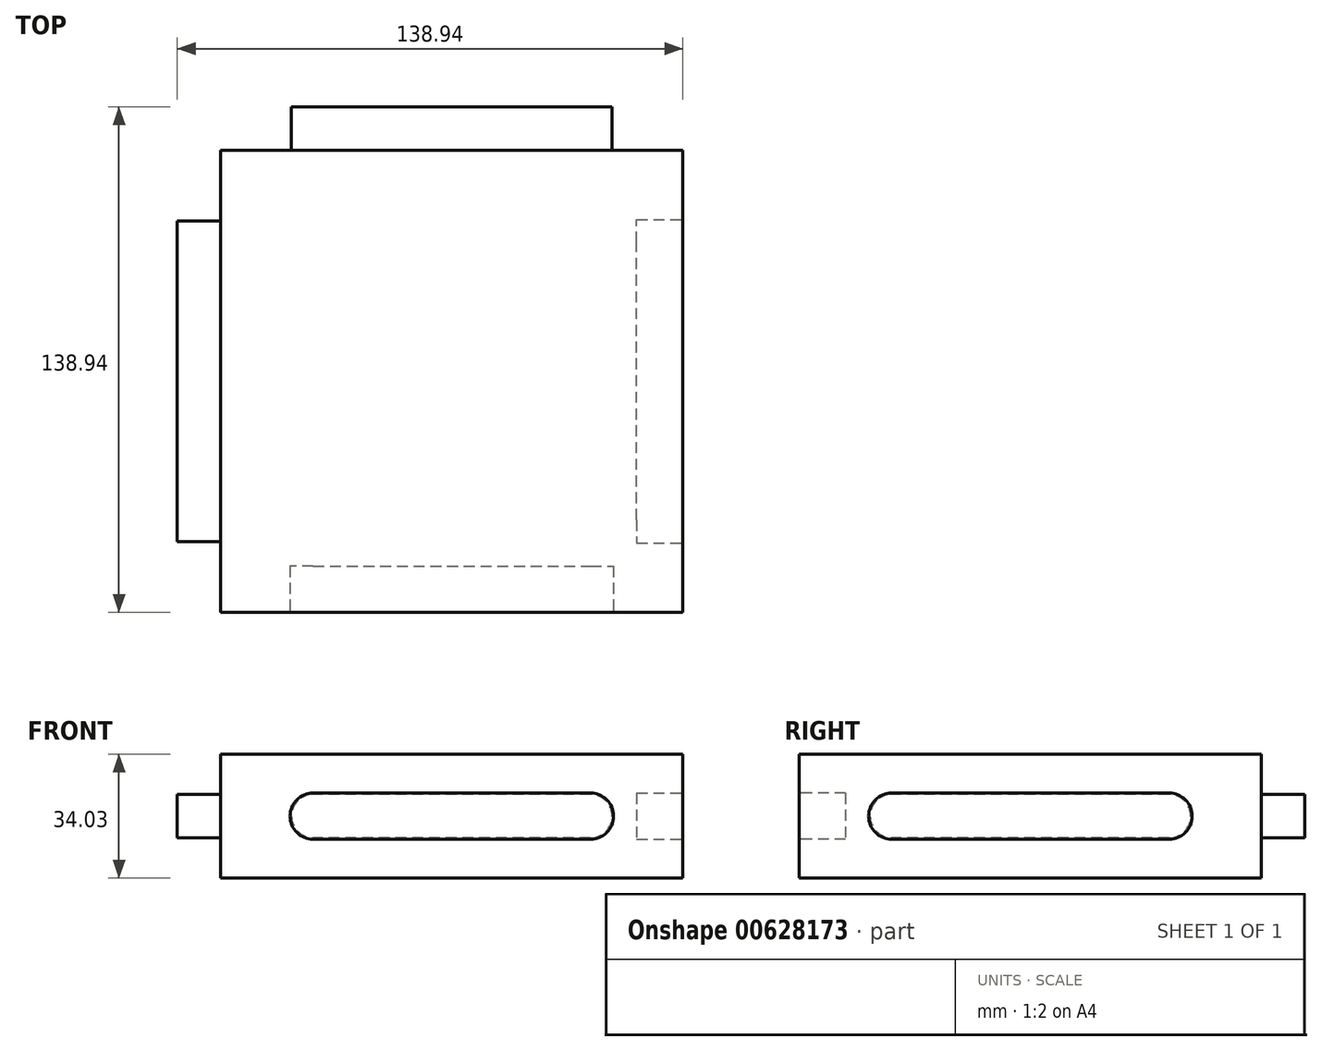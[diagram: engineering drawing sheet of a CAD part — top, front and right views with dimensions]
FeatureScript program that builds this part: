
annotation { "Feature Type Name" : "Feature", "Feature Type Description" : "" }
export const myFeature = defineFeature(function(context is Context, id is Id, definition is map)
    precondition{}
    {
        {
            var Q0;
            Q0=qCreatedBy(makeId("Top.planeOp"),FACE);
            var sketch = newSketch(context, id + "F0", { "sketchPlane" : qUnion([Q0])});
            skLineSegment(sketch, "E0.bottom", {"start": v(-63.5, 63.5) * mm, "end": v(63.5, 63.5) * mm});
            skLineSegment(sketch, "E0.top", {"start": v(-63.5, -63.5) * mm, "end": v(63.5, -63.5) * mm});
            skLineSegment(sketch, "E0.left", {"start": v(-63.5, 63.5) * mm, "end": v(-63.5, -63.5) * mm});
            skLineSegment(sketch, "E0.right", {"start": v(63.5, 63.5) * mm, "end": v(63.5, -63.5) * mm});
            skSolve(sketch);
        }
        {
            var Q0;
            Q0 = qSketchRegion(id + "F0", true);
            extrude(context, id + "F1", {"entities" : qUnion([Q0]), "depth" : 34.03 * mm, "offsetDistance" : 25.4 * mm});
        }
        {
            var Q0;
            Q0=makeQuery(id+"F1.opExtrude","SWEPT_FACE",FACE,{"disambiguationData":[OSD([sQuery(id+"F0.wireOp",EDGE,"E0.bottom")])]});
            var sketch = newSketch(context, id + "F2", { "sketchPlane" : qUnion([Q0])});
            skLineSegment(sketch, "E1", {"start": v(-63.5, 17.01) * mm, "end": v(-38.1, 17.01) * mm, "construction": true});
            skLineSegment(sketch, "E2", {"start": v(63.5, 17.01) * mm, "end": v(38.1, 17.01) * mm, "construction": true});
            skLineSegment(sketch, "E3", {"start": v(-38.1, 17.01) * mm, "end": v(38.1, 17.01) * mm, "construction": true});
            skArc(sketch, "E4.0.startCap", {"start": v(-38.1, 11.05) * mm, "mid": v(-44.07, 17.01) * mm, "end": v(-38.1, 22.98) * mm});
            skArc(sketch, "E4.0.endCap", {"start": v(38.1, 22.98) * mm, "mid": v(44.07, 17.01) * mm, "end": v(38.1, 11.05) * mm});
            skLineSegment(sketch, "E4.0.left", {"start": v(-38.1, 22.98) * mm, "end": v(38.1, 22.98) * mm});
            skLineSegment(sketch, "E4.0.right", {"start": v(-38.1, 11.05) * mm, "end": v(38.1, 11.05) * mm});
            skSolve(sketch);
        }
        {
            var Q0;
            Q0 = qSketchRegion(id + "F2", true);
            extrude(context, id + "F3", {"entities" : qUnion([Q0]), "operationType" : NewBodyOperationType.ADD, "depth" : 11.94 * mm, "offsetDistance" : 25.4 * mm});
        }
        {
            var Q0;
            Q0=makeQuery(id+"F1.opExtrude","SWEPT_FACE",FACE,{"disambiguationData":[OSD([sQuery(id+"F0.wireOp",EDGE,"E0.right")])]});
            var sketch = newSketch(context, id + "F4", { "sketchPlane" : qUnion([Q0])});
            skLineSegment(sketch, "E5", {"start": v(-63.5, 17.01) * mm, "end": v(-38.1, 17.01) * mm, "construction": true});
            skLineSegment(sketch, "E6", {"start": v(63.5, 17.01) * mm, "end": v(38.1, 17.01) * mm, "construction": true});
            skLineSegment(sketch, "E7", {"start": v(-38.1, 17.01) * mm, "end": v(38.1, 17.01) * mm, "construction": true});
            skArc(sketch, "E8.0.startCap", {"start": v(-38.1, 10.66) * mm, "mid": v(-44.45, 17.01) * mm, "end": v(-38.1, 23.36) * mm});
            skArc(sketch, "E8.0.endCap", {"start": v(38.1, 23.36) * mm, "mid": v(44.45, 17.01) * mm, "end": v(38.1, 10.66) * mm});
            skLineSegment(sketch, "E8.0.left", {"start": v(-38.1, 23.36) * mm, "end": v(38.1, 23.36) * mm});
            skLineSegment(sketch, "E8.0.right", {"start": v(-38.1, 10.66) * mm, "end": v(38.1, 10.66) * mm});
            skSolve(sketch);
        }
        {
            var Q0;
            Q0=makeQuery(id+"F1.opExtrude","SWEPT_FACE",FACE,{"disambiguationData":[OSD([sQuery(id+"F0.wireOp",EDGE,"E0.top")])]});
            var sketch = newSketch(context, id + "F5", { "sketchPlane" : qUnion([Q0])});
            skLineSegment(sketch, "E9", {"start": v(-63.5, 17.01) * mm, "end": v(-38.1, 17.01) * mm, "construction": true});
            skLineSegment(sketch, "E10", {"start": v(63.5, 17.01) * mm, "end": v(38.1, 17.01) * mm, "construction": true});
            skLineSegment(sketch, "E11", {"start": v(-38.1, 17.01) * mm, "end": v(38.1, 17.01) * mm, "construction": true});
            skArc(sketch, "E12.0.startCap", {"start": v(-38.1, 10.66) * mm, "mid": v(-44.45, 17.01) * mm, "end": v(-38.1, 23.36) * mm});
            skArc(sketch, "E12.0.endCap", {"start": v(38.1, 23.36) * mm, "mid": v(44.45, 17.01) * mm, "end": v(38.1, 10.66) * mm});
            skLineSegment(sketch, "E12.0.left", {"start": v(-38.1, 23.36) * mm, "end": v(38.1, 23.36) * mm});
            skLineSegment(sketch, "E12.0.right", {"start": v(-38.1, 10.66) * mm, "end": v(38.1, 10.66) * mm});
            skSolve(sketch);
        }
        {
            var Q0;
            Q0 = qSketchRegion(id + "F4", true);
            extrude(context, id + "F6", {"entities" : qUnion([Q0]), "operationType" : NewBodyOperationType.REMOVE, "oppositeDirection" : true, "depth" : 12.7 * mm, "offsetDistance" : 25.4 * mm});
        }
        {
            var Q0;
            Q0 = qSketchRegion(id + "F5", true);
            extrude(context, id + "F7", {"entities" : qUnion([Q0]), "operationType" : NewBodyOperationType.REMOVE, "oppositeDirection" : true, "depth" : 12.7 * mm, "offsetDistance" : 25.4 * mm});
        }
        {
            var Q0;
            Q0=makeQuery(id+"F1.opExtrude","SWEPT_FACE",FACE,{"disambiguationData":[OSD([sQuery(id+"F0.wireOp",EDGE,"E0.left")])]});
            var sketch = newSketch(context, id + "F8", { "sketchPlane" : qUnion([Q0])});
            skLineSegment(sketch, "E13", {"start": v(-63.5, 17.01) * mm, "end": v(-38.1, 17.01) * mm, "construction": true});
            skLineSegment(sketch, "E14", {"start": v(63.5, 17.01) * mm, "end": v(38.1, 17.01) * mm, "construction": true});
            skLineSegment(sketch, "E15", {"start": v(-38.1, 17.01) * mm, "end": v(38.1, 17.01) * mm, "construction": true});
            skArc(sketch, "E16.0.startCap", {"start": v(-38.1, 11.05) * mm, "mid": v(-44.07, 17.01) * mm, "end": v(-38.1, 22.98) * mm});
            skArc(sketch, "E16.0.endCap", {"start": v(38.1, 22.98) * mm, "mid": v(44.07, 17.01) * mm, "end": v(38.1, 11.05) * mm});
            skLineSegment(sketch, "E16.0.left", {"start": v(-38.1, 22.98) * mm, "end": v(38.1, 22.98) * mm});
            skLineSegment(sketch, "E16.0.right", {"start": v(-38.1, 11.05) * mm, "end": v(38.1, 11.05) * mm});
            skSolve(sketch);
        }
        {
            var Q0;
            Q0 = qSketchRegion(id + "F8", true);
            extrude(context, id + "F9", {"entities" : qUnion([Q0]), "operationType" : NewBodyOperationType.ADD, "depth" : 11.94 * mm, "offsetDistance" : 25.4 * mm});
        }
    });
